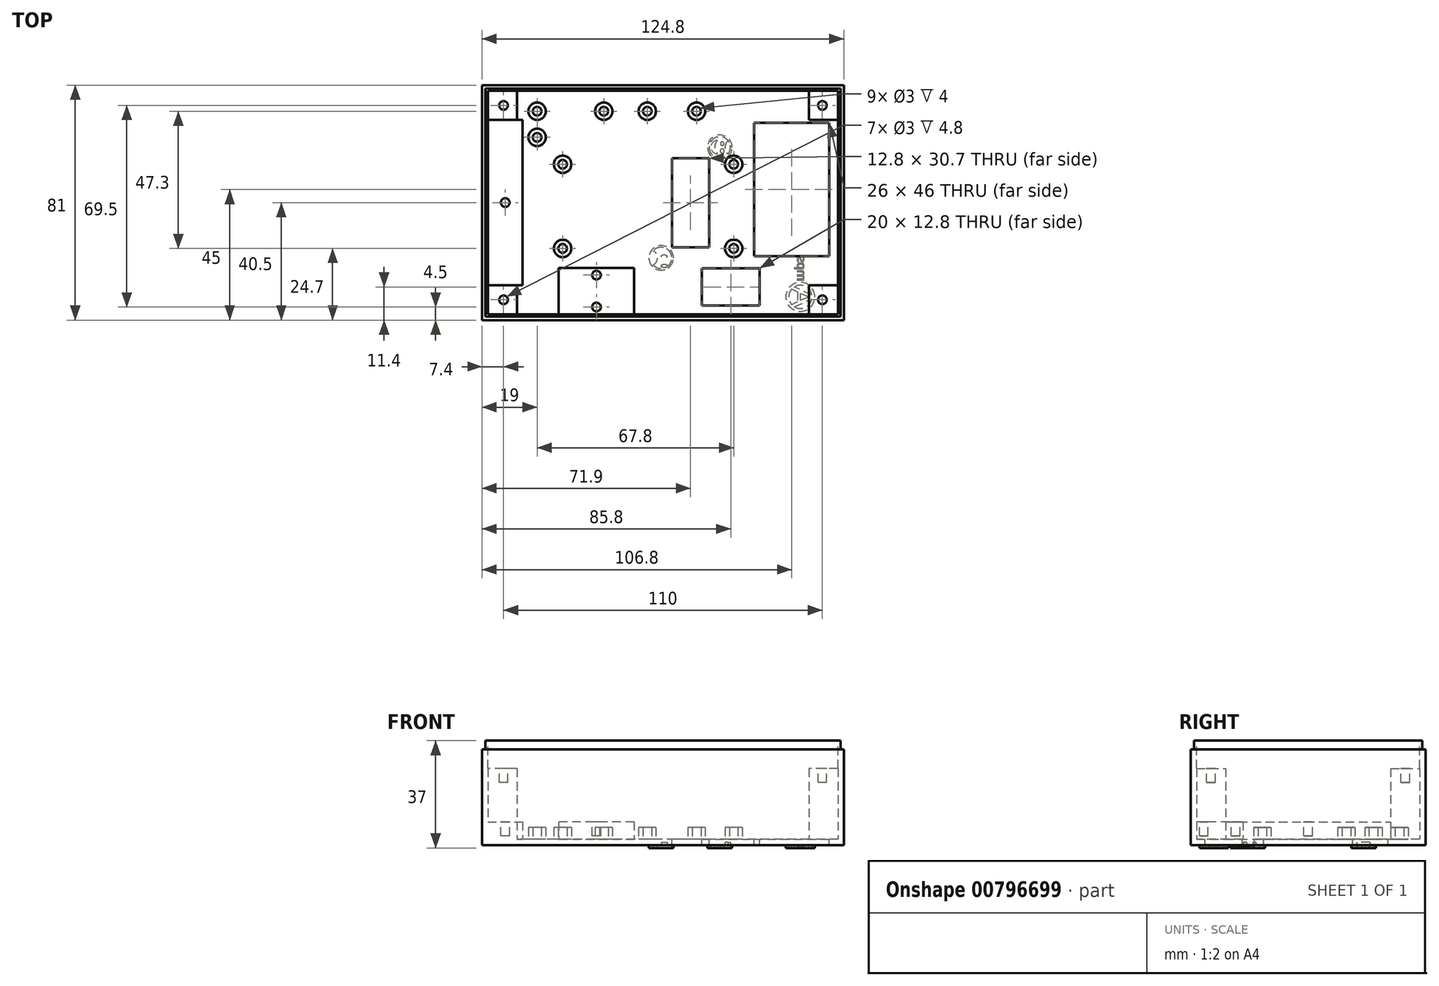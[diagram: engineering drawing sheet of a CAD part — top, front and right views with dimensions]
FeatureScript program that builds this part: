
annotation { "Feature Type Name" : "Feature", "Feature Type Description" : "" }
export const myFeature = defineFeature(function(context is Context, id is Id, definition is map)
    precondition{}
    {
        {
            var Q0;
            Q0=qCreatedBy(makeId("Top.planeOp"),FACE);
            var sketch = newSketch(context, id + "F0", { "sketchPlane" : qUnion([Q0])});
            skLineSegment(sketch, "E0.bottom", {"start": v(62.4, -40.5) * mm, "end": v(-62.4, -40.5) * mm});
            skLineSegment(sketch, "E0.top", {"start": v(62.4, 40.5) * mm, "end": v(-62.4, 40.5) * mm});
            skLineSegment(sketch, "E0.left", {"start": v(62.4, -40.5) * mm, "end": v(62.4, 40.5) * mm});
            skLineSegment(sketch, "E0.right", {"start": v(-62.4, -40.5) * mm, "end": v(-62.4, 40.5) * mm});
            skPoint(sketch, "E0.middle", {"position": v(0, 0) * mm});
            skSolve(sketch);
        }
        {
            var Q0;
            Q0=qSketchRegion(id+"F0",true);
            extrude(context, id + "F1", {"entities" : qUnion([Q0]), "depth" : 33 * mm, "offsetDistance" : 25 * mm});
        }
        {
            var Q0;
            Q0=makeQuery(id+"F1.opExtrude","CAP_FACE",FACE,{"disambiguationData":[OSD([sQuery(id+"F0.wireOp",EDGE,"E0.bottom"),sQuery(id+"F0.wireOp",EDGE,"E0.top"),sQuery(id+"F0.wireOp",EDGE,"E0.left"),sQuery(id+"F0.wireOp",EDGE,"E0.right")])],"isStart":false});
            var sketch = newSketch(context, id + "F2", { "sketchPlane" : qUnion([Q0])});
            skLineSegment(sketch, "E1.bottom", {"start": v(61.25, -39.35) * mm, "end": v(-61.25, -39.35) * mm});
            skLineSegment(sketch, "E1.top", {"start": v(61.25, 39.35) * mm, "end": v(-61.25, 39.35) * mm});
            skLineSegment(sketch, "E1.left", {"start": v(61.25, -39.35) * mm, "end": v(61.25, 39.35) * mm});
            skLineSegment(sketch, "E1.right", {"start": v(-61.25, -39.35) * mm, "end": v(-61.25, 39.35) * mm});
            skPoint(sketch, "E1.middle", {"position": v(0, 0) * mm});
            skSolve(sketch);
        }
        {
            var Q0;
            Q0=qSketchRegion(id+"F2",true);
            extrude(context, id + "F3", {"entities" : qUnion([Q0]), "operationType" : NewBodyOperationType.ADD, "depth" : 3 * mm, "offsetDistance" : 25 * mm});
        }
        {
            var Q0;
            Q0=makeQuery(id+"F3.opExtrude","CAP_FACE",FACE,{"disambiguationData":[OSD([sQuery(id+"F2.wireOp",EDGE,"E1.bottom"),sQuery(id+"F2.wireOp",EDGE,"E1.top"),sQuery(id+"F2.wireOp",EDGE,"E1.left"),sQuery(id+"F2.wireOp",EDGE,"E1.right")])],"isStart":false});
            var sketch = newSketch(context, id + "F4", { "sketchPlane" : qUnion([Q0])});
            skLineSegment(sketch, "E2.bottom", {"start": v(60.4, -38.5) * mm, "end": v(-60.4, -38.5) * mm});
            skLineSegment(sketch, "E2.top", {"start": v(60.4, 38.5) * mm, "end": v(-60.4, 38.5) * mm});
            skLineSegment(sketch, "E2.left", {"start": v(60.4, -38.5) * mm, "end": v(60.4, 38.5) * mm});
            skLineSegment(sketch, "E2.right", {"start": v(-60.4, -38.5) * mm, "end": v(-60.4, 38.5) * mm});
            skPoint(sketch, "E2.middle", {"position": v(0, 0) * mm});
            skSolve(sketch);
        }
        {
            var Q0;
            Q0=qSketchRegion(id+"F4",true);
            extrude(context, id + "F5", {"entities" : qUnion([Q0]), "operationType" : NewBodyOperationType.REMOVE, "oppositeDirection" : true, "depth" : 34 * mm, "offsetDistance" : 25 * mm});
        }
        {
            var Q0;
            Q0=makeQuery(id+"F5.boolean.opBoolean","COPY",FACE,{"derivedFrom":makeQuery(id+"F5.opExtrude","CAP_FACE",FACE,{"disambiguationData":[OSD([sQuery(id+"F4.wireOp",EDGE,"E2.bottom"),sQuery(id+"F4.wireOp",EDGE,"E2.top"),sQuery(id+"F4.wireOp",EDGE,"E2.left"),sQuery(id+"F4.wireOp",EDGE,"E2.right")])],"isStart":false})});
            var sketch = newSketch(context, id + "F6", { "sketchPlane" : qUnion([Q0])});
            skLineSegment(sketch, "E3.bottom", {"start": v(-60.4, 38.5) * mm, "end": v(-50.4, 38.5) * mm});
            skLineSegment(sketch, "E3.top", {"start": v(-60.4, 28.5) * mm, "end": v(-50.4, 28.5) * mm});
            skLineSegment(sketch, "E3.left", {"start": v(-60.4, 38.5) * mm, "end": v(-60.4, 28.5) * mm});
            skLineSegment(sketch, "E3.right", {"start": v(-50.4, 38.5) * mm, "end": v(-50.4, 28.5) * mm});
            skLineSegment(sketch, "E4.bottom", {"start": v(-60.4, -38.5) * mm, "end": v(-50.4, -38.5) * mm});
            skLineSegment(sketch, "E4.top", {"start": v(-60.4, -28.5) * mm, "end": v(-50.4, -28.5) * mm});
            skLineSegment(sketch, "E4.left", {"start": v(-60.4, -38.5) * mm, "end": v(-60.4, -28.5) * mm});
            skLineSegment(sketch, "E4.right", {"start": v(-50.4, -38.5) * mm, "end": v(-50.4, -28.5) * mm});
            skLineSegment(sketch, "E5.bottom", {"start": v(60.4, -38.5) * mm, "end": v(50.4, -38.5) * mm});
            skLineSegment(sketch, "E5.top", {"start": v(60.4, -28.5) * mm, "end": v(50.4, -28.5) * mm});
            skLineSegment(sketch, "E5.left", {"start": v(60.4, -38.5) * mm, "end": v(60.4, -28.5) * mm});
            skLineSegment(sketch, "E5.right", {"start": v(50.4, -38.5) * mm, "end": v(50.4, -28.5) * mm});
            skLineSegment(sketch, "E6.bottom", {"start": v(60.4, 38.5) * mm, "end": v(50.4, 38.5) * mm});
            skLineSegment(sketch, "E6.top", {"start": v(60.4, 28.5) * mm, "end": v(50.4, 28.5) * mm});
            skLineSegment(sketch, "E6.left", {"start": v(60.4, 38.5) * mm, "end": v(60.4, 28.5) * mm});
            skLineSegment(sketch, "E6.right", {"start": v(50.4, 38.5) * mm, "end": v(50.4, 28.5) * mm});
            skSolve(sketch);
        }
        {
            var Q0;
            Q0=qSketchRegion(id+"F6",true);
            extrude(context, id + "F7", {"entities" : qUnion([Q0]), "operationType" : NewBodyOperationType.ADD, "depth" : 24.4 * mm, "offsetDistance" : 25 * mm});
        }
        {
            var Q0;
            Q0=makeQuery(id+"F7.opExtrude","CAP_FACE",FACE,{"disambiguationData":[OSD([sQuery(id+"F6.wireOp",EDGE,"E3.bottom"),sQuery(id+"F6.wireOp",EDGE,"E3.top"),sQuery(id+"F6.wireOp",EDGE,"E3.left"),sQuery(id+"F6.wireOp",EDGE,"E3.right")])],"isStart":false});
            var sketch = newSketch(context, id + "F8", { "sketchPlane" : qUnion([Q0])});
            skCircle(sketch, "E7", {"center": v(-55, 33.5) * mm, "radius": 1.5 * mm});
            skPoint(sketch, "E7.centerSnap0", {"position": v(-50.4, 33.5) * mm});
            skCircle(sketch, "E8", {"center": v(-55, -33.5) * mm, "radius": 1.5 * mm});
            skCircle(sketch, "E9", {"center": v(55, -33.5) * mm, "radius": 1.5 * mm});
            skCircle(sketch, "E10", {"center": v(55, 33.5) * mm, "radius": 1.5 * mm});
            skSolve(sketch);
        }
        {
            var Q0;
            Q0=qSketchRegion(id+"F8",true);
            extrude(context, id + "F9", {"entities" : qUnion([Q0]), "operationType" : NewBodyOperationType.REMOVE, "oppositeDirection" : true, "depth" : 4.8 * mm, "offsetDistance" : 25 * mm});
        }
        {
            var Q0;
            Q0=makeQuery(id+"F5.boolean.opBoolean","COPY",FACE,{"derivedFrom":makeQuery(id+"F5.opExtrude","CAP_FACE",FACE,{"disambiguationData":[OSD([sQuery(id+"F4.wireOp",EDGE,"E2.bottom"),sQuery(id+"F4.wireOp",EDGE,"E2.top"),sQuery(id+"F4.wireOp",EDGE,"E2.left"),sQuery(id+"F4.wireOp",EDGE,"E2.right")])],"isStart":false})});
            var sketch = newSketch(context, id + "F10", { "sketchPlane" : qUnion([Q0])});
            skLineSegment(sketch, "E11.bottom", {"start": v(31.4, 27.5) * mm, "end": v(57.4, 27.5) * mm});
            skLineSegment(sketch, "E11.top", {"start": v(31.4, -18.5) * mm, "end": v(57.4, -18.5) * mm});
            skLineSegment(sketch, "E11.left", {"start": v(31.4, 27.5) * mm, "end": v(31.4, -18.5) * mm});
            skLineSegment(sketch, "E11.right", {"start": v(57.4, 27.5) * mm, "end": v(57.4, -18.5) * mm});
            skLineSegment(sketch, "E12.bottom", {"start": v(13.4, -22.7) * mm, "end": v(33.4, -22.7) * mm});
            skLineSegment(sketch, "E12.top", {"start": v(13.4, -35.5) * mm, "end": v(33.4, -35.5) * mm});
            skLineSegment(sketch, "E12.left", {"start": v(13.4, -22.7) * mm, "end": v(13.4, -35.5) * mm});
            skLineSegment(sketch, "E12.right", {"start": v(33.4, -22.7) * mm, "end": v(33.4, -35.5) * mm});
            skLineSegment(sketch, "E13.bottom", {"start": v(15.9, -15.35) * mm, "end": v(3.1, -15.35) * mm});
            skLineSegment(sketch, "E13.top", {"start": v(15.9, 15.35) * mm, "end": v(3.1, 15.35) * mm});
            skLineSegment(sketch, "E13.left", {"start": v(15.9, -15.35) * mm, "end": v(15.9, 15.35) * mm});
            skLineSegment(sketch, "E13.right", {"start": v(3.1, -15.35) * mm, "end": v(3.1, 15.35) * mm});
            skPoint(sketch, "E13.middle", {"position": v(9.5, 0) * mm});
            skSolve(sketch);
        }
        {
            var Q0;
            Q0=qSketchRegion(id+"F10",true);
            extrude(context, id + "F11", {"entities" : qUnion([Q0]), "operationType" : NewBodyOperationType.REMOVE, "endBound" : BoundingType.THROUGH_ALL, "oppositeDirection" : true, "depth" : 25 * mm, "offsetDistance" : 25 * mm});
        }
        {
            var Q0;
            Q0=makeQuery(id+"F5.boolean.opBoolean","COPY",FACE,{"derivedFrom":makeQuery(id+"F5.opExtrude","CAP_FACE",FACE,{"disambiguationData":[OSD([sQuery(id+"F4.wireOp",EDGE,"E2.bottom"),sQuery(id+"F4.wireOp",EDGE,"E2.top"),sQuery(id+"F4.wireOp",EDGE,"E2.left"),sQuery(id+"F4.wireOp",EDGE,"E2.right")])],"isStart":false})});
            var sketch = newSketch(context, id + "F12", { "sketchPlane" : qUnion([Q0])});
            skCircle(sketch, "E14", {"center": v(24.4, 13.2) * mm, "radius": 3 * mm});
            skCircle(sketch, "E15", {"center": v(-34.6, 13.2) * mm, "radius": 3 * mm});
            skCircle(sketch, "E16", {"center": v(-34.6, -15.8) * mm, "radius": 3 * mm});
            skCircle(sketch, "E17", {"center": v(24.4, -15.8) * mm, "radius": 3 * mm});
            skCircle(sketch, "E18", {"center": v(-43.4, 31.5) * mm, "radius": 3 * mm});
            skCircle(sketch, "E19", {"center": v(-43.4, 22.5) * mm, "radius": 3 * mm});
            skCircle(sketch, "E20", {"center": v(-20.4, 31.5) * mm, "radius": 3 * mm});
            skCircle(sketch, "E21", {"center": v(-5.4, 31.5) * mm, "radius": 3 * mm});
            skCircle(sketch, "E22", {"center": v(11.6, 31.5) * mm, "radius": 3 * mm});
            skSolve(sketch);
        }
        {
            var Q0;
            Q0=qSketchRegion(id+"F12",true);
            extrude(context, id + "F13", {"entities" : qUnion([Q0]), "operationType" : NewBodyOperationType.ADD, "depth" : 4 * mm, "offsetDistance" : 25 * mm});
        }
        {
            var Q0;
            Q0=makeQuery(id+"F5.boolean.opBoolean","COPY",FACE,{"derivedFrom":makeQuery(id+"F5.opExtrude","CAP_FACE",FACE,{"disambiguationData":[OSD([sQuery(id+"F4.wireOp",EDGE,"E2.bottom"),sQuery(id+"F4.wireOp",EDGE,"E2.top"),sQuery(id+"F4.wireOp",EDGE,"E2.left"),sQuery(id+"F4.wireOp",EDGE,"E2.right")])],"isStart":false})});
            var sketch = newSketch(context, id + "F14", { "sketchPlane" : qUnion([Q0])});
            skCircle(sketch, "E23", {"center": v(-34.6, -15.8) * mm, "radius": 1.5 * mm});
            skCircle(sketch, "E24", {"center": v(24.4, -15.8) * mm, "radius": 1.5 * mm});
            skCircle(sketch, "E25", {"center": v(-34.6, 13.2) * mm, "radius": 1.5 * mm});
            skCircle(sketch, "E26", {"center": v(24.4, 13.2) * mm, "radius": 1.5 * mm});
            skCircle(sketch, "E27", {"center": v(11.6, 31.5) * mm, "radius": 1.5 * mm});
            skCircle(sketch, "E28", {"center": v(-5.4, 31.5) * mm, "radius": 1.5 * mm});
            skCircle(sketch, "E29", {"center": v(-20.4, 31.5) * mm, "radius": 1.5 * mm});
            skCircle(sketch, "E30", {"center": v(-43.4, 22.5) * mm, "radius": 1.5 * mm});
            skCircle(sketch, "E31", {"center": v(-43.4, 31.5) * mm, "radius": 1.5 * mm});
            skSolve(sketch);
        }
        {
            var Q0;
            Q0=qSketchRegion(id+"F14",true);
            extrude(context, id + "F15", {"entities" : qUnion([Q0]), "operationType" : NewBodyOperationType.REMOVE, "depth" : 4.8 * mm, "offsetDistance" : 25 * mm});
        }
        {
            var Q0;
            Q0=makeQuery(id+"F5.boolean.opBoolean","COPY",FACE,{"derivedFrom":makeQuery(id+"F5.opExtrude","CAP_FACE",FACE,{"disambiguationData":[OSD([sQuery(id+"F4.wireOp",EDGE,"E2.bottom"),sQuery(id+"F4.wireOp",EDGE,"E2.top"),sQuery(id+"F4.wireOp",EDGE,"E2.left"),sQuery(id+"F4.wireOp",EDGE,"E2.right")])],"isStart":false})});
            var sketch = newSketch(context, id + "F16", { "sketchPlane" : qUnion([Q0])});
            skLineSegment(sketch, "E32.bottom", {"start": v(-60.4, -28.5) * mm, "end": v(-48.4, -28.5) * mm});
            skLineSegment(sketch, "E32.top", {"start": v(-60.4, 28.5) * mm, "end": v(-48.4, 28.5) * mm});
            skLineSegment(sketch, "E32.left", {"start": v(-60.4, -28.5) * mm, "end": v(-60.4, 28.5) * mm});
            skLineSegment(sketch, "E32.right", {"start": v(-48.4, -28.5) * mm, "end": v(-48.4, 28.5) * mm});
            skSolve(sketch);
        }
        {
            var Q0;
            Q0=qSketchRegion(id+"F16",true);
            extrude(context, id + "F17", {"entities" : qUnion([Q0]), "operationType" : NewBodyOperationType.ADD, "depth" : 6 * mm, "offsetDistance" : 25 * mm});
        }
        {
            var Q0;
            Q0=makeQuery(id+"F17.opExtrude","CAP_FACE",FACE,{"disambiguationData":[OSD([sQuery(id+"F16.wireOp",EDGE,"E32.bottom"),sQuery(id+"F16.wireOp",EDGE,"E32.top"),sQuery(id+"F16.wireOp",EDGE,"E32.left"),sQuery(id+"F16.wireOp",EDGE,"E32.right")])],"isStart":false});
            var sketch = newSketch(context, id + "F18", { "sketchPlane" : qUnion([Q0])});
            skCircle(sketch, "E33", {"center": v(-54.4, 0) * mm, "radius": 1.5 * mm});
            skPoint(sketch, "E33.centerSnap0", {"position": v(-48.4, 0) * mm});
            skSolve(sketch);
        }
        {
            var Q0;
            Q0=qSketchRegion(id+"F18",true);
            extrude(context, id + "F19", {"entities" : qUnion([Q0]), "operationType" : NewBodyOperationType.REMOVE, "oppositeDirection" : true, "depth" : 4.8 * mm, "offsetDistance" : 25 * mm});
        }
        {
            var Q0;
            Q0=makeQuery(id+"F5.boolean.opBoolean","COPY",FACE,{"derivedFrom":makeQuery(id+"F5.opExtrude","CAP_FACE",FACE,{"disambiguationData":[OSD([sQuery(id+"F4.wireOp",EDGE,"E2.bottom"),sQuery(id+"F4.wireOp",EDGE,"E2.top"),sQuery(id+"F4.wireOp",EDGE,"E2.left"),sQuery(id+"F4.wireOp",EDGE,"E2.right")])],"isStart":false})});
            var sketch = newSketch(context, id + "F20", { "sketchPlane" : qUnion([Q0])});
            skLineSegment(sketch, "E34.bottom", {"start": v(-35.93, -22.5) * mm, "end": v(-9.93, -22.5) * mm});
            skLineSegment(sketch, "E34.top", {"start": v(-35.93, -38.5) * mm, "end": v(-9.93, -38.5) * mm});
            skLineSegment(sketch, "E34.left", {"start": v(-35.93, -22.5) * mm, "end": v(-35.93, -38.5) * mm});
            skLineSegment(sketch, "E34.right", {"start": v(-9.93, -22.5) * mm, "end": v(-9.93, -38.5) * mm});
            skSolve(sketch);
        }
        {
            var Q0;
            Q0=qSketchRegion(id+"F20",true);
            extrude(context, id + "F21", {"entities" : qUnion([Q0]), "operationType" : NewBodyOperationType.ADD, "depth" : 6 * mm, "offsetDistance" : 25 * mm});
        }
        {
            var Q0;
            Q0=makeQuery(id+"F21.opExtrude","CAP_FACE",FACE,{"disambiguationData":[OSD([sQuery(id+"F20.wireOp",EDGE,"E34.bottom"),sQuery(id+"F20.wireOp",EDGE,"E34.top"),sQuery(id+"F20.wireOp",EDGE,"E34.left"),sQuery(id+"F20.wireOp",EDGE,"E34.right")])],"isStart":false});
            var sketch = newSketch(context, id + "F22", { "sketchPlane" : qUnion([Q0])});
            skCircle(sketch, "E35", {"center": v(-22.93, -25) * mm, "radius": 1.5 * mm});
            skPoint(sketch, "E35.centerSnap0", {"position": v(-22.93, -22.5) * mm});
            skPoint(sketch, "E35.perimeterSnap0", {"position": v(-22.93, -22.5) * mm});
            skPoint(sketch, "E35.perimeterSnap1", {"position": v(-35.93, -30.5) * mm});
            skCircle(sketch, "E36", {"center": v(-22.93, -36) * mm, "radius": 1.5 * mm});
            skSolve(sketch);
        }
        {
            var Q0;
            Q0=qSketchRegion(id+"F22",true);
            extrude(context, id + "F23", {"entities" : qUnion([Q0]), "operationType" : NewBodyOperationType.REMOVE, "oppositeDirection" : true, "depth" : 4.8 * mm, "offsetDistance" : 25 * mm});
        }
        {
            var Q0;
            Q0=makeQuery(id+"F1.opExtrude","CAP_FACE",FACE,{"disambiguationData":[OSD([sQuery(id+"F0.wireOp",EDGE,"E0.bottom"),sQuery(id+"F0.wireOp",EDGE,"E0.top"),sQuery(id+"F0.wireOp",EDGE,"E0.left"),sQuery(id+"F0.wireOp",EDGE,"E0.right")])],"isStart":true});
            var sketch = newSketch(context, id + "F24", { "sketchPlane" : qUnion([Q0])});
            skCircle(sketch, "E37", {"center": v(47.4, 32.5) * mm, "radius": 5 * mm});
            skCircle(sketch, "E38", {"center": v(47.4, 32.5) * mm, "radius": 4 * mm});
            skSolve(sketch);
        }
        {
            var Q0;
            Q0=qSketchRegion(id+"F24",true);
            extrude(context, id + "F25", {"entities" : qUnion([Q0]), "operationType" : NewBodyOperationType.ADD, "depth" : 1 * mm, "offsetDistance" : 25 * mm});
        }
        {
            var Q0;
            {var subQ0=sQuery(id+"F0.wireOp",EDGE,"E0.bottom");var subQ1=sQuery(id+"F0.wireOp",EDGE,"E0.right");var subQ2=sQuery(id+"F0.wireOp",EDGE,"E0.top");var subQ3=sQuery(id+"F0.wireOp",EDGE,"E0.left");Q0=makeQuery(id+"F25.boolean.opBoolean","SPLIT",FACE,{"disambiguationData":[TD([makeQuery(id+"F1.opExtrude","SWEPT_FACE",FACE,{"disambiguationData":[OSD([subQ0])]})])],"derivedFrom":makeQuery(id+"F1.opExtrude","CAP_FACE",FACE,{"disambiguationData":[OSD([subQ0,subQ2,subQ3,subQ1])],"isStart":true})});}
            var sketch = newSketch(context, id + "F26", { "sketchPlane" : qUnion([Q0])});
            skText(sketch, "E39", { "text": "mps", "fontName": "OpenSans-Regular.ttf"});
            const initialGuessF26  = {"E39": [0.04636, 0.0271, 0, -1, 0.00304]};
            skSetInitialGuess(sketch, initialGuessF26);
            skSolve(sketch);
        }
        {
            var Q0;
            Q0=qSketchRegion(id+"F26",true);
            extrude(context, id + "F27", {"entities" : qUnion([Q0]), "operationType" : NewBodyOperationType.ADD, "depth" : 1 * mm, "offsetDistance" : 25 * mm});
        }
        {
            var Q0;
            {var subQ12=sQuery(id+"F0.wireOp",EDGE,"E0.right");var subQ14=sQuery(id+"F0.wireOp",EDGE,"E0.top");var subQ16=sQuery(id+"F0.wireOp",EDGE,"E0.left");var subQ18=sQuery(id+"F0.wireOp",EDGE,"E0.bottom");var subQ19=makeQuery(id+"F1.opExtrude","SWEPT_FACE",FACE,{"disambiguationData":[OSD([subQ18])]});Q0=makeQuery(id+"F27.boolean.opBoolean","SPLIT",FACE,{"disambiguationData":[TD([subQ19])],"derivedFrom":makeQuery(id+"F25.boolean.opBoolean","SPLIT",FACE,{"disambiguationData":[TD([subQ19])],"derivedFrom":makeQuery(id+"F1.opExtrude","CAP_FACE",FACE,{"disambiguationData":[OSD([subQ18,subQ14,subQ16,subQ12])],"isStart":true})})});}
            var sketch = newSketch(context, id + "F28", { "sketchPlane" : qUnion([Q0])});
            skLineSegment(sketch, "E40", {"start": v(44.91, 36.12) * mm, "end": v(51.52, 33.06) * mm});
            skLineSegment(sketch, "E41", {"start": v(51.52, 33.06) * mm, "end": v(51.52, 31.97) * mm});
            skLineSegment(sketch, "E42", {"start": v(51.52, 31.97) * mm, "end": v(45.1, 28.97) * mm});
            skLineSegment(sketch, "E43", {"start": v(45.1, 28.97) * mm, "end": v(44.19, 29.7) * mm});
            skLineSegment(sketch, "E44", {"start": v(44.19, 29.7) * mm, "end": v(46.4, 30.75) * mm});
            skLineSegment(sketch, "E45", {"start": v(46.4, 30.75) * mm, "end": v(46.4, 34.26) * mm});
            skLineSegment(sketch, "E46", {"start": v(46.4, 34.26) * mm, "end": v(44.17, 35.3) * mm});
            skLineSegment(sketch, "E47", {"start": v(44.17, 35.3) * mm, "end": v(44.91, 36.12) * mm});
            skLineSegment(sketch, "E48", {"start": v(50.23, 32.5) * mm, "end": v(47.48, 33.76) * mm});
            skLineSegment(sketch, "E49", {"start": v(47.48, 33.76) * mm, "end": v(47.48, 31.24) * mm});
            skLineSegment(sketch, "E50", {"start": v(47.48, 31.24) * mm, "end": v(50.23, 32.5) * mm});
            skSolve(sketch);
        }
        {
            var Q0;
            Q0=makeQuery(id+"F28.imprint","IMPRINT",FACE,{"disambiguationData":[TD([[makeQuery(id+"F28.imprint","IMPRINT",EDGE,{"derivedFrom":sQuery(id+"F28.wireOp",EDGE,"E40")}),-1.0]])]});
            extrude(context, id + "F29", {"entities" : qUnion([Q0]), "operationType" : NewBodyOperationType.ADD, "depth" : 1 * mm, "offsetDistance" : 25 * mm});
        }
        {
            var Q0;
            {var subQ12=sQuery(id+"F0.wireOp",EDGE,"E0.right");var subQ14=sQuery(id+"F0.wireOp",EDGE,"E0.top");var subQ16=sQuery(id+"F0.wireOp",EDGE,"E0.left");var subQ18=sQuery(id+"F0.wireOp",EDGE,"E0.bottom");var subQ19=makeQuery(id+"F1.opExtrude","SWEPT_FACE",FACE,{"disambiguationData":[OSD([subQ18])]});Q0=makeQuery(id+"F27.boolean.opBoolean","SPLIT",FACE,{"disambiguationData":[TD([subQ19])],"derivedFrom":makeQuery(id+"F25.boolean.opBoolean","SPLIT",FACE,{"disambiguationData":[TD([subQ19])],"derivedFrom":makeQuery(id+"F1.opExtrude","CAP_FACE",FACE,{"disambiguationData":[OSD([subQ18,subQ14,subQ16,subQ12])],"isStart":true})})});}
            var sketch = newSketch(context, id + "F30", { "sketchPlane" : qUnion([Q0])});
            skCircle(sketch, "E51", {"center": v(19.61, -19.06) * mm, "radius": 4.25 * mm});
            skCircle(sketch, "E52", {"center": v(-0.61, 19.06) * mm, "radius": 4.25 * mm});
            skLineSegment(sketch, "E53", {"start": v(15.9, -15.35) * mm, "end": v(19.61, -19.06) * mm, "construction": true});
            skLineSegment(sketch, "E54", {"start": v(3.1, 15.35) * mm, "end": v(-0.61, 19.06) * mm, "construction": true});
            skCircle(sketch, "E55", {"center": v(-0.61, 19.06) * mm, "radius": 3.65 * mm});
            skCircle(sketch, "E56", {"center": v(19.61, -19.06) * mm, "radius": 3.65 * mm});
            skSolve(sketch);
        }
        {
            var Q0;
            Q0=qSketchRegion(id+"F30",true);
            extrude(context, id + "F31", {"entities" : qUnion([Q0]), "operationType" : NewBodyOperationType.ADD, "depth" : 1 * mm, "offsetDistance" : 25 * mm});
        }
        {
            var Q0;
            {var subQ34=sQuery(id+"F0.wireOp",EDGE,"E0.right");var subQ38=sQuery(id+"F0.wireOp",EDGE,"E0.top");var subQ42=sQuery(id+"F0.wireOp",EDGE,"E0.left");var subQ47=sQuery(id+"F0.wireOp",EDGE,"E0.bottom");var subQ48=makeQuery(id+"F1.opExtrude","SWEPT_FACE",FACE,{"disambiguationData":[OSD([subQ47])]});Q0=makeQuery(id+"F31.boolean.opBoolean","SPLIT",FACE,{"disambiguationData":[TD([subQ48])],"derivedFrom":makeQuery(id+"F27.boolean.opBoolean","SPLIT",FACE,{"disambiguationData":[TD([subQ48])],"derivedFrom":makeQuery(id+"F25.boolean.opBoolean","SPLIT",FACE,{"disambiguationData":[TD([subQ48])],"derivedFrom":makeQuery(id+"F1.opExtrude","CAP_FACE",FACE,{"disambiguationData":[OSD([subQ47,subQ38,subQ42,subQ34])],"isStart":true})})})});}
            var sketch = newSketch(context, id + "F32", { "sketchPlane" : qUnion([Q0])});
            skArc(sketch, "E57", {"start": v(22.46, -16.78) * mm, "mid": v(21.42, -19.05) * mm, "end": v(22.46, -21.32) * mm});
            skArc(sketch, "E58", {"start": v(22.46, -21.32) * mm, "mid": v(23.3, -19.05) * mm, "end": v(22.46, -16.78) * mm});
            skSolve(sketch);
        }
        {
            var Q0;
            Q0=qSketchRegion(id+"F32",true);
            extrude(context, id + "F33", {"entities" : qUnion([Q0]), "operationType" : NewBodyOperationType.REMOVE, "oppositeDirection" : true, "depth" : 1 * mm, "offsetDistance" : 25 * mm});
        }
        {
            var Q0;
            {var subQ34=sQuery(id+"F0.wireOp",EDGE,"E0.right");var subQ38=sQuery(id+"F0.wireOp",EDGE,"E0.top");var subQ42=sQuery(id+"F0.wireOp",EDGE,"E0.left");var subQ47=sQuery(id+"F0.wireOp",EDGE,"E0.bottom");var subQ48=makeQuery(id+"F1.opExtrude","SWEPT_FACE",FACE,{"disambiguationData":[OSD([subQ47])]});Q0=makeQuery(id+"F31.boolean.opBoolean","SPLIT",FACE,{"disambiguationData":[TD([subQ48])],"derivedFrom":makeQuery(id+"F27.boolean.opBoolean","SPLIT",FACE,{"disambiguationData":[TD([subQ48])],"derivedFrom":makeQuery(id+"F25.boolean.opBoolean","SPLIT",FACE,{"disambiguationData":[TD([subQ48])],"derivedFrom":makeQuery(id+"F1.opExtrude","CAP_FACE",FACE,{"disambiguationData":[OSD([subQ47,subQ38,subQ42,subQ34])],"isStart":true})})})});}
            var sketch = newSketch(context, id + "F34", { "sketchPlane" : qUnion([Q0])});
            skArc(sketch, "E59", {"start": v(-3.67, 16.54) * mm, "mid": v(-1.88, 19.07) * mm, "end": v(-3.67, 21.6) * mm});
            skArc(sketch, "E60", {"start": v(-3.67, 21.6) * mm, "mid": v(-4.55, 19.07) * mm, "end": v(-3.67, 16.54) * mm});
            skSolve(sketch);
        }
        {
            var Q0;
            Q0=qSketchRegion(id+"F34",true);
            extrude(context, id + "F35", {"entities" : qUnion([Q0]), "operationType" : NewBodyOperationType.ADD, "depth" : 1 * mm, "offsetDistance" : 25 * mm});
        }
        {
            var Q0;
            {var subQ34=sQuery(id+"F0.wireOp",EDGE,"E0.right");var subQ38=sQuery(id+"F0.wireOp",EDGE,"E0.top");var subQ42=sQuery(id+"F0.wireOp",EDGE,"E0.left");var subQ47=sQuery(id+"F0.wireOp",EDGE,"E0.bottom");var subQ48=makeQuery(id+"F1.opExtrude","SWEPT_FACE",FACE,{"disambiguationData":[OSD([subQ47])]});Q0=makeQuery(id+"F31.boolean.opBoolean","SPLIT",FACE,{"disambiguationData":[TD([subQ48])],"derivedFrom":makeQuery(id+"F27.boolean.opBoolean","SPLIT",FACE,{"disambiguationData":[TD([subQ48])],"derivedFrom":makeQuery(id+"F25.boolean.opBoolean","SPLIT",FACE,{"disambiguationData":[TD([subQ48])],"derivedFrom":makeQuery(id+"F1.opExtrude","CAP_FACE",FACE,{"disambiguationData":[OSD([subQ47,subQ38,subQ42,subQ34])],"isStart":true})})})});}
            var sketch = newSketch(context, id + "F36", { "sketchPlane" : qUnion([Q0])});
            skEllipse(sketch, "E61", {"center": v(0.46, 21.82) * mm, "majorRadius": 1.05 * mm, "minorRadius": 0.58 * mm, "majorAxis": v(-1, 0)});
            skEllipse(sketch, "E62", {"center": v(0.46, 18.5) * mm, "majorRadius": 1 * mm, "minorRadius": 0.5 * mm, "majorAxis": v(-1, 0)});
            skSolve(sketch);
        }
        {
            var Q0;
            Q0=qSketchRegion(id+"F36",true);
            extrude(context, id + "F37", {"entities" : qUnion([Q0]), "operationType" : NewBodyOperationType.REMOVE, "oppositeDirection" : true, "depth" : 1 * mm, "offsetDistance" : 25 * mm});
        }
        {
            var Q0;
            {var subQ34=sQuery(id+"F0.wireOp",EDGE,"E0.right");var subQ38=sQuery(id+"F0.wireOp",EDGE,"E0.top");var subQ42=sQuery(id+"F0.wireOp",EDGE,"E0.left");var subQ47=sQuery(id+"F0.wireOp",EDGE,"E0.bottom");var subQ48=makeQuery(id+"F1.opExtrude","SWEPT_FACE",FACE,{"disambiguationData":[OSD([subQ47])]});Q0=makeQuery(id+"F31.boolean.opBoolean","SPLIT",FACE,{"disambiguationData":[TD([subQ48])],"derivedFrom":makeQuery(id+"F27.boolean.opBoolean","SPLIT",FACE,{"disambiguationData":[TD([subQ48])],"derivedFrom":makeQuery(id+"F25.boolean.opBoolean","SPLIT",FACE,{"disambiguationData":[TD([subQ48])],"derivedFrom":makeQuery(id+"F1.opExtrude","CAP_FACE",FACE,{"disambiguationData":[OSD([subQ47,subQ38,subQ42,subQ34])],"isStart":true})})})});}
            var sketch = newSketch(context, id + "F38", { "sketchPlane" : qUnion([Q0])});
            skCircle(sketch, "E63", {"center": v(20.46, -17.82) * mm, "radius": 0.7 * mm});
            skCircle(sketch, "E64", {"center": v(20.46, -20.33) * mm, "radius": 0.62 * mm});
            skArc(sketch, "E65", {"start": v(18.9, -16.8) * mm, "mid": v(16.55, -19.13) * mm, "end": v(18.9, -21.48) * mm});
            skArc(sketch, "E66", {"start": v(18.9, -16.8) * mm, "mid": v(17.9, -19.13) * mm, "end": v(18.9, -21.48) * mm});
            skSolve(sketch);
        }
        {
            var Q0;
            Q0=qSketchRegion(id+"F38",true);
            extrude(context, id + "F39", {"entities" : qUnion([Q0]), "operationType" : NewBodyOperationType.ADD, "depth" : 1 * mm, "offsetDistance" : 25 * mm});
        }
    });
